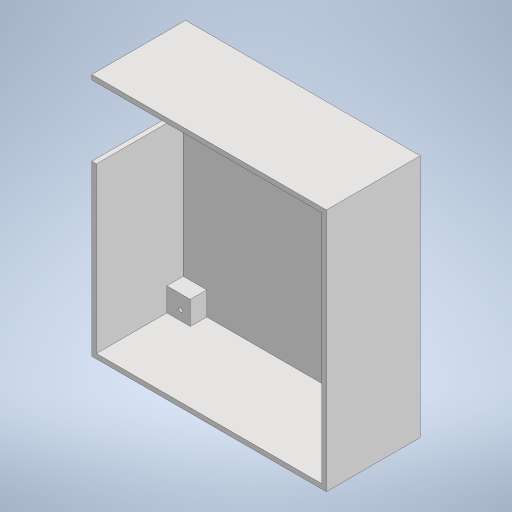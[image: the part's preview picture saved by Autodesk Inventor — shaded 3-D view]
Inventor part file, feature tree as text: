
AUTODESK INVENTOR PART (.ipt)
format: ipt  version: 2024.1 (Build 281209000, 209)  size: 267,264 bytes
history: native  units: in
note: dims shown in document units (in); Inventor stores cm internally (conversion verified against a paired STEP export)
features: extrude x6, sketch x6
ambient origin geometry x8: Origin, YZ Plane, XZ Plane, XY Plane, X Axis, Y Axis, Z Axis, Center Point
bodies: Solid1 (feature_tree)
feature tree (12):
  extrude  "Extrusion1"  Depth=4.0945in
  extrude  "Extrusion2"  Depth=0.0787in
  extrude  "Extrusion3"  Depth=0.0787in
  extrude  "Extrusion4"  Depth=1.4567in TaperAngle=0.0deg
  extrude  "Extrusion5"  Depth=0.3937in
  extrude  "Extrusion6"  Depth=0.3937in
  sketch  "Sketch1"  dims[d0=3.937in d1=4.0945in]
  sketch  "Sketch2"  dims[d2=1.5748in d3=0.0in d4=0.0787in]
  sketch  "Sketch3"  dims[d5=0.0787in d6=0.0787in]
  sketch  "Sketch4"  dims[d7=0.0787in d8=1.4567in d9=0.0in]
  sketch  "Sketch5"  dims[d10=0.3937in d11=0.3937in]
  sketch  "Sketch6"  dims[d12=0.3937in d13=0.3937in d14=0.3937in d15=0.3937in d16=0.3937in d17=0.3937in d18=0.2756in d19=0.0in d20=1.1811in d21=0.1969in d22=0.0in d23=0.7874in d24=0.2756in d25=0.0in d26=0.063in d27=0.063in d28=0.063in d29=0.063in d30=0.1575in d31=0.2313in d32=0.1575in d33=0.2313in d34=0.2313in d35=0.2313in d36=0.1575in d37=0.1575in d38=0.0in d39=0.0in]
